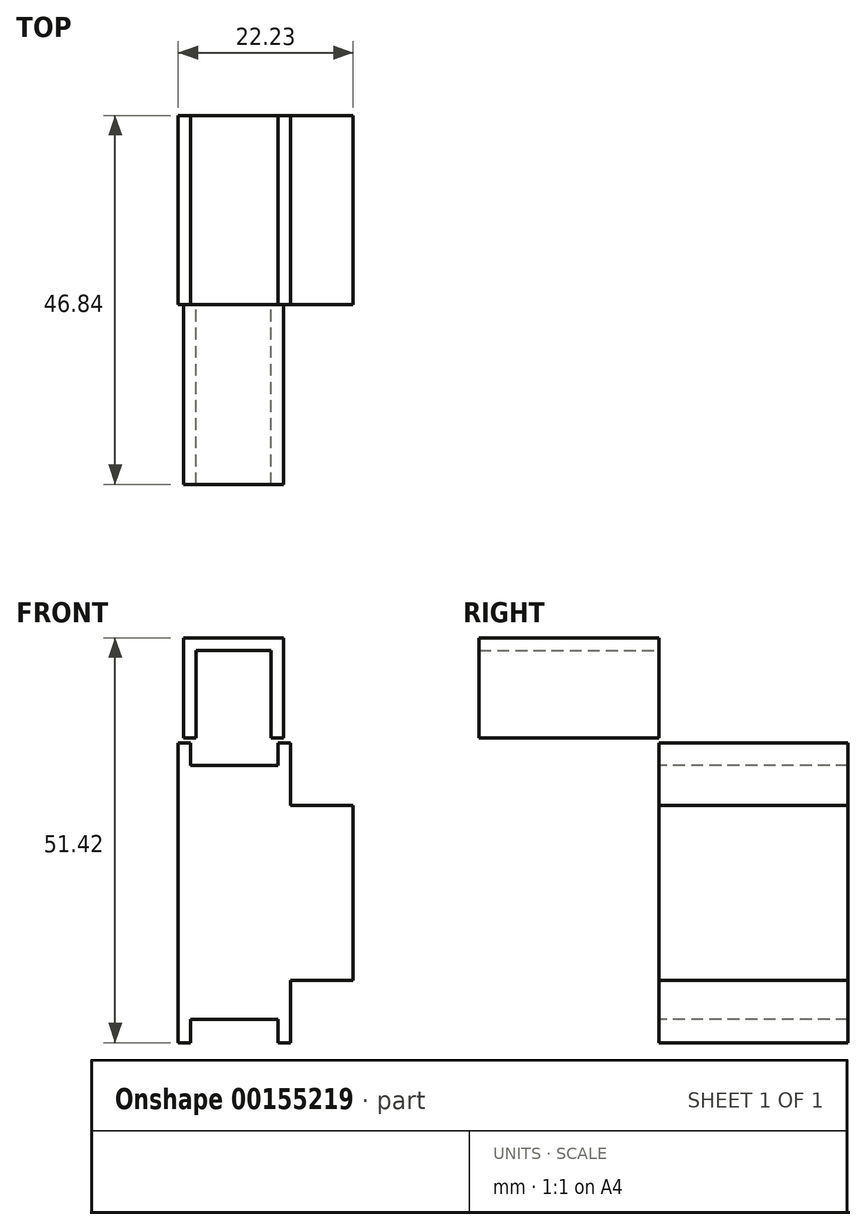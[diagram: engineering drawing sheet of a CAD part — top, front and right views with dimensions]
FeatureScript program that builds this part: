
annotation { "Feature Type Name" : "Feature", "Feature Type Description" : "" }
export const myFeature = defineFeature(function(context is Context, id is Id, definition is map)
    precondition{}
    {
        {
            var Q0;
            Q0=qCreatedBy(makeId("Front.planeOp"),FACE);
            var sketch = newSketch(context, id + "F0", { "sketchPlane" : qUnion([Q0])});
            skLineSegment(sketch, "E0.bottom", {"start": v(0, 0) * mm, "end": v(-7.94, 0) * mm});
            skLineSegment(sketch, "E0.top", {"start": v(0, -22.22) * mm, "end": v(-7.94, -22.22) * mm});
            skLineSegment(sketch, "E0.left", {"start": v(0, 0) * mm, "end": v(0, -22.22) * mm});
            skLineSegment(sketch, "E0.right", {"start": v(-7.94, 0) * mm, "end": v(-7.94, -22.22) * mm});
            skLineSegment(sketch, "E1", {"start": v(-7.94, 0) * mm, "end": v(-7.94, 7.94) * mm});
            skLineSegment(sketch, "E2", {"start": v(-7.94, -22.22) * mm, "end": v(-7.94, -30.16) * mm});
            skLineSegment(sketch, "E3", {"start": v(-7.94, 7.94) * mm, "end": v(-9.53, 7.94) * mm});
            skLineSegment(sketch, "E4", {"start": v(-7.94, -30.16) * mm, "end": v(-9.52, -30.16) * mm});
            skLineSegment(sketch, "E5", {"start": v(-9.53, 7.94) * mm, "end": v(-9.52, -30.16) * mm});
            skLineSegment(sketch, "E6", {"start": v(-9.53, 5.08) * mm, "end": v(-20.64, 5.08) * mm});
            skLineSegment(sketch, "E7", {"start": v(-9.52, -27.2) * mm, "end": v(-20.64, -27.2) * mm});
            skLineSegment(sketch, "E8", {"start": v(-20.64, 5.08) * mm, "end": v(-20.64, 2.93) * mm});
            skLineSegment(sketch, "E9", {"start": v(-20.64, 7.94) * mm, "end": v(-23.4, 7.94) * mm});
            skLineSegment(sketch, "E10", {"start": v(-20.64, 7.94) * mm, "end": v(-20.64, 5.08) * mm});
            skLineSegment(sketch, "E11", {"start": v(-22.23, 2.93) * mm, "end": v(-22.23, -8.84) * mm});
            skLineSegment(sketch, "E12", {"start": v(-22.23, -8.84) * mm, "end": v(-22.23, -16.38) * mm});
            skLineSegment(sketch, "E13", {"start": v(-22.22, -16.38) * mm, "end": v(-22.22, -27.2) * mm});
            skLineSegment(sketch, "E14", {"start": v(-20.64, -27.2) * mm, "end": v(-22.22, -27.2) * mm});
            skLineSegment(sketch, "E15", {"start": v(-22.23, 2.93) * mm, "end": v(-22.23, 7.94) * mm});
            skLineSegment(sketch, "E16", {"start": v(-20.64, 7.94) * mm, "end": v(-22.23, 7.94) * mm});
            skPoint(sketch, "E17.start.orphan", {"position": v(-20.64, -16.38) * mm});
            skLineSegment(sketch, "E18.trimOffspring", {"start": v(-20.64, -8.84) * mm, "end": v(-20.64, -27.2) * mm});
            skLineSegment(sketch, "E19", {"start": v(-20.64, 2.93) * mm, "end": v(-20.64, -8.84) * mm});
            skLineSegment(sketch, "E20", {"start": v(-20.64, -30.16) * mm, "end": v(-22.22, -30.16) * mm});
            skLineSegment(sketch, "E21", {"start": v(-20.64, -27.2) * mm, "end": v(-20.64, -30.16) * mm});
            skLineSegment(sketch, "E22", {"start": v(-22.22, -27.2) * mm, "end": v(-22.22, -30.16) * mm});
            skSolve(sketch);
        }
        {
            var Q0;
            Q0=qCreatedBy(makeId("Front.planeOp"),FACE);
            var sketch = newSketch(context, id + "F1", { "sketchPlane" : qUnion([Q0])});
            skLineSegment(sketch, "E23.top", {"start": v(-8.87, 21.26) * mm, "end": v(-21.57, 21.26) * mm});
            skLineSegment(sketch, "E23.left", {"start": v(-8.87, 8.56) * mm, "end": v(-8.87, 21.26) * mm});
            skLineSegment(sketch, "E23.right", {"start": v(-21.57, 8.56) * mm, "end": v(-21.57, 21.26) * mm});
            skLineSegment(sketch, "E24", {"start": v(-17.8, 19.67) * mm, "end": v(-10.46, 19.67) * mm});
            skLineSegment(sketch, "E25", {"start": v(-17.8, 19.67) * mm, "end": v(-19.98, 19.67) * mm});
            skLineSegment(sketch, "E26", {"start": v(-19.98, 11.12) * mm, "end": v(-19.98, 8.56) * mm});
            skLineSegment(sketch, "E27", {"start": v(-19.98, 14.9) * mm, "end": v(-19.98, 11.12) * mm});
            skLineSegment(sketch, "E28", {"start": v(-19.98, 14.9) * mm, "end": v(-19.98, 19.67) * mm});
            skPoint(sketch, "E29.start.orphan", {"position": v(-21.57, 14.9) * mm});
            skLineSegment(sketch, "E30", {"start": v(-10.46, 14.9) * mm, "end": v(-10.46, 9.3) * mm});
            skLineSegment(sketch, "E31", {"start": v(-10.46, 14.9) * mm, "end": v(-10.46, 19.67) * mm});
            skPoint(sketch, "E32.start.orphan", {"position": v(-8.87, 14.9) * mm});
            skLineSegment(sketch, "E33", {"start": v(-10.46, 9.3) * mm, "end": v(-10.46, 8.56) * mm});
            skLineSegment(sketch, "E34", {"start": v(-10.46, 8.56) * mm, "end": v(-8.87, 8.56) * mm});
            skLineSegment(sketch, "E35", {"start": v(-19.98, 8.56) * mm, "end": v(-21.57, 8.56) * mm});
            skSolve(sketch);
        }
        {
            var Q0;
            Q0=makeQuery(id+"F1.imprint","IMPRINT",FACE,{"disambiguationData":[TD([[makeQuery(id+"F1.imprint","IMPRINT",EDGE,{"derivedFrom":sQuery(id+"F1.wireOp",EDGE,"E23.top")}),1.0]])]});
            extrude(context, id + "F2", {"entities" : qUnion([Q0]), "depth" : 0.03 * yard});
        }
        {
            var Q0;
            Q0=makeQuery(id+"F0.imprint","IMPRINT",FACE,{"disambiguationData":[TD([[makeQuery(id+"F0.imprint","IMPRINT",EDGE,{"derivedFrom":sQuery(id+"F0.wireOp",EDGE,"E0.right")}),-1.0]])]});
            var Q1;
            Q1=makeQuery(id+"F0.imprint","IMPRINT",FACE,{"disambiguationData":[TD([[makeQuery(id+"F0.imprint","IMPRINT",EDGE,{"derivedFrom":sQuery(id+"F0.wireOp",EDGE,"E0.bottom")}),1.0]])]});
            var Q2;
            {var subQ1=sQuery(id+"F0.wireOp",EDGE,"E6");Q2=makeQuery(id+"F0.imprint","IMPRINT",FACE,{"disambiguationData":[TD([[makeQuery(id+"F0.imprint","IMPRINT",EDGE,{"derivedFrom":subQ1}),1.0]])]});}
            var Q3;
            Q3=makeQuery(id+"F0.imprint","IMPRINT",FACE,{"disambiguationData":[TD([[makeQuery(id+"F0.imprint","IMPRINT",EDGE,{"derivedFrom":sQuery(id+"F0.wireOp",EDGE,"E8")}),-1.0]])]});
            var Q4;
            Q4=makeQuery(id+"F0.imprint","IMPRINT",FACE,{"disambiguationData":[TD([[makeQuery(id+"F0.imprint","IMPRINT",EDGE,{"derivedFrom":sQuery(id+"F0.wireOp",EDGE,"E14")}),1.0]])]});
            extrude(context, id + "F3", {"entities" : qUnion([Q0, Q1, Q2, Q3, Q4]), "oppositeDirection" : true, "depth" : 23.98 * mm});
        }
    });
